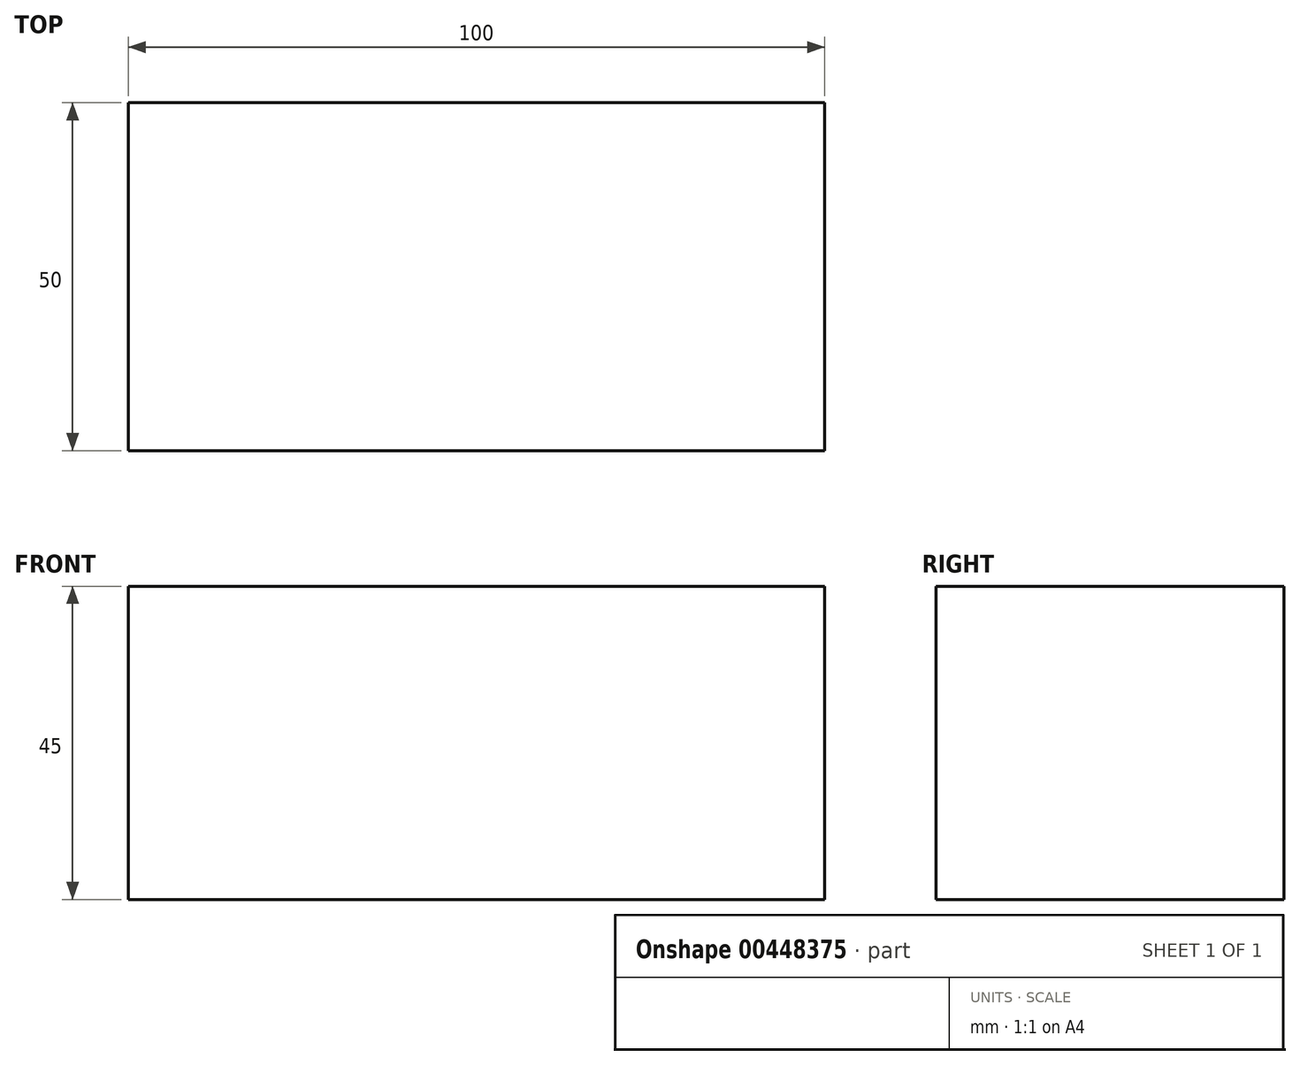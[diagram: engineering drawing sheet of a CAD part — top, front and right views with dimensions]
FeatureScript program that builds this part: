
annotation { "Feature Type Name" : "Feature", "Feature Type Description" : "" }
export const myFeature = defineFeature(function(context is Context, id is Id, definition is map)
    precondition{}
    {
        {
            var Q0;
            Q0=qCreatedBy(makeId("Front.planeOp"),FACE);
            var sketch = newSketch(context, id + "F0", { "sketchPlane" : qUnion([Q0])});
            skLineSegment(sketch, "E0", {"start": v(0, 0) * mm, "end": v(53.34, 0) * mm, "construction": true});
            skLineSegment(sketch, "E1", {"start": v(0, 0) * mm, "end": v(0, 52.9) * mm, "construction": true});
            skLineSegment(sketch, "E2.bottom", {"start": v(-50, 22.5) * mm, "end": v(50, 22.5) * mm});
            skLineSegment(sketch, "E2.top", {"start": v(-50, -22.5) * mm, "end": v(50, -22.5) * mm});
            skLineSegment(sketch, "E2.left", {"start": v(-50, 22.5) * mm, "end": v(-50, -22.5) * mm});
            skLineSegment(sketch, "E2.right", {"start": v(50, 22.5) * mm, "end": v(50, -22.5) * mm});
            skSolve(sketch);
        }
        {
            var Q0;
            Q0 = qSketchRegion(id + "F0", true);
            extrude(context, id + "F1", {"entities" : qUnion([Q0]), "depth" : 25 * mm, "hasSecondDirection" : true, "secondDirectionOppositeDirection" : true, "secondDirectionDepth" : 25 * mm});
        }
    });
